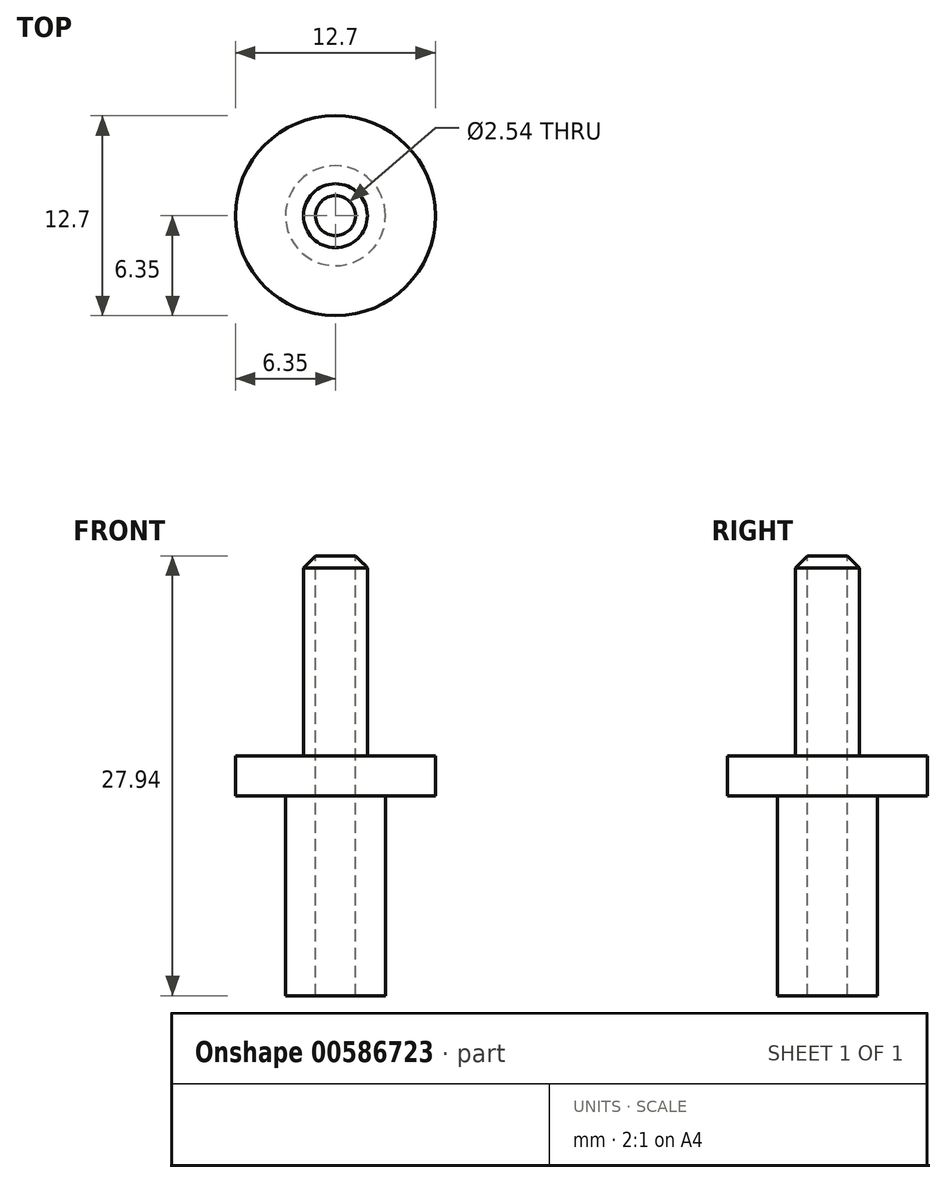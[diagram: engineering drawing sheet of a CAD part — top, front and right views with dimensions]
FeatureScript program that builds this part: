
annotation { "Feature Type Name" : "Feature", "Feature Type Description" : "" }
export const myFeature = defineFeature(function(context is Context, id is Id, definition is map)
    precondition{}
    {
        {
            var Q0;
            Q0=qCreatedBy(makeId("Front.planeOp"),FACE);
            var sketch = newSketch(context, id + "F0", { "sketchPlane" : qUnion([Q0])});
            skLineSegment(sketch, "E0", {"start": v(1.27, 0) * mm, "end": v(1.27, -13.97) * mm});
            skLineSegment(sketch, "E1", {"start": v(1.27, 0) * mm, "end": v(2.03, 0) * mm});
            skLineSegment(sketch, "E2", {"start": v(2.03, 0) * mm, "end": v(2.03, -12.7) * mm});
            skLineSegment(sketch, "E3", {"start": v(2.03, -12.7) * mm, "end": v(6.35, -12.7) * mm});
            skLineSegment(sketch, "E4", {"start": v(6.35, -12.7) * mm, "end": v(6.35, -15.24) * mm});
            skLineSegment(sketch, "E5", {"start": v(6.35, -15.24) * mm, "end": v(3.17, -15.24) * mm});
            skLineSegment(sketch, "E6", {"start": v(3.17, -15.24) * mm, "end": v(3.18, -27.94) * mm});
            skLineSegment(sketch, "E7", {"start": v(3.18, -27.94) * mm, "end": v(1.27, -27.94) * mm});
            skLineSegment(sketch, "E8", {"start": v(1.27, -27.94) * mm, "end": v(1.27, -13.97) * mm});
            skLineSegment(sketch, "E9", {"start": v(0, 0) * mm, "end": v(0, -37.65) * mm, "construction": true});
            skSolve(sketch);
        }
        {
            var Q0;
            Q0=makeQuery(id+"F0.imprint","IMPRINT",FACE,{"disambiguationData":[TD([[makeQuery(id+"F0.imprint","IMPRINT",EDGE,{"derivedFrom":sQuery(id+"F0.wireOp",EDGE,"E0")}),1.0]])]});
            var Q1;
            Q1=sQuery(id+"F0.wireOp",EDGE,"E9");
            revolve(context, id + "F1", {"entities" : qUnion([Q0]), "axis" : qUnion([Q1]), "revolveType" : RevolveType.FULL});
        }
        {
            var Q0;
            Q0=makeQuery(id+"F1.opRevolve","SWEPT_EDGE",EDGE,{"disambiguationData":[OSD([sQuery(id+"F0.wireOp",EDGE,"E1"),sQuery(id+"F0.wireOp",EDGE,"E2")])]});
            chamfer(context, id + "F2", {"entities" : qUnion([Q0]), "width" : 0.76 * mm, "tangentPropagation" : true});
        }
    });
